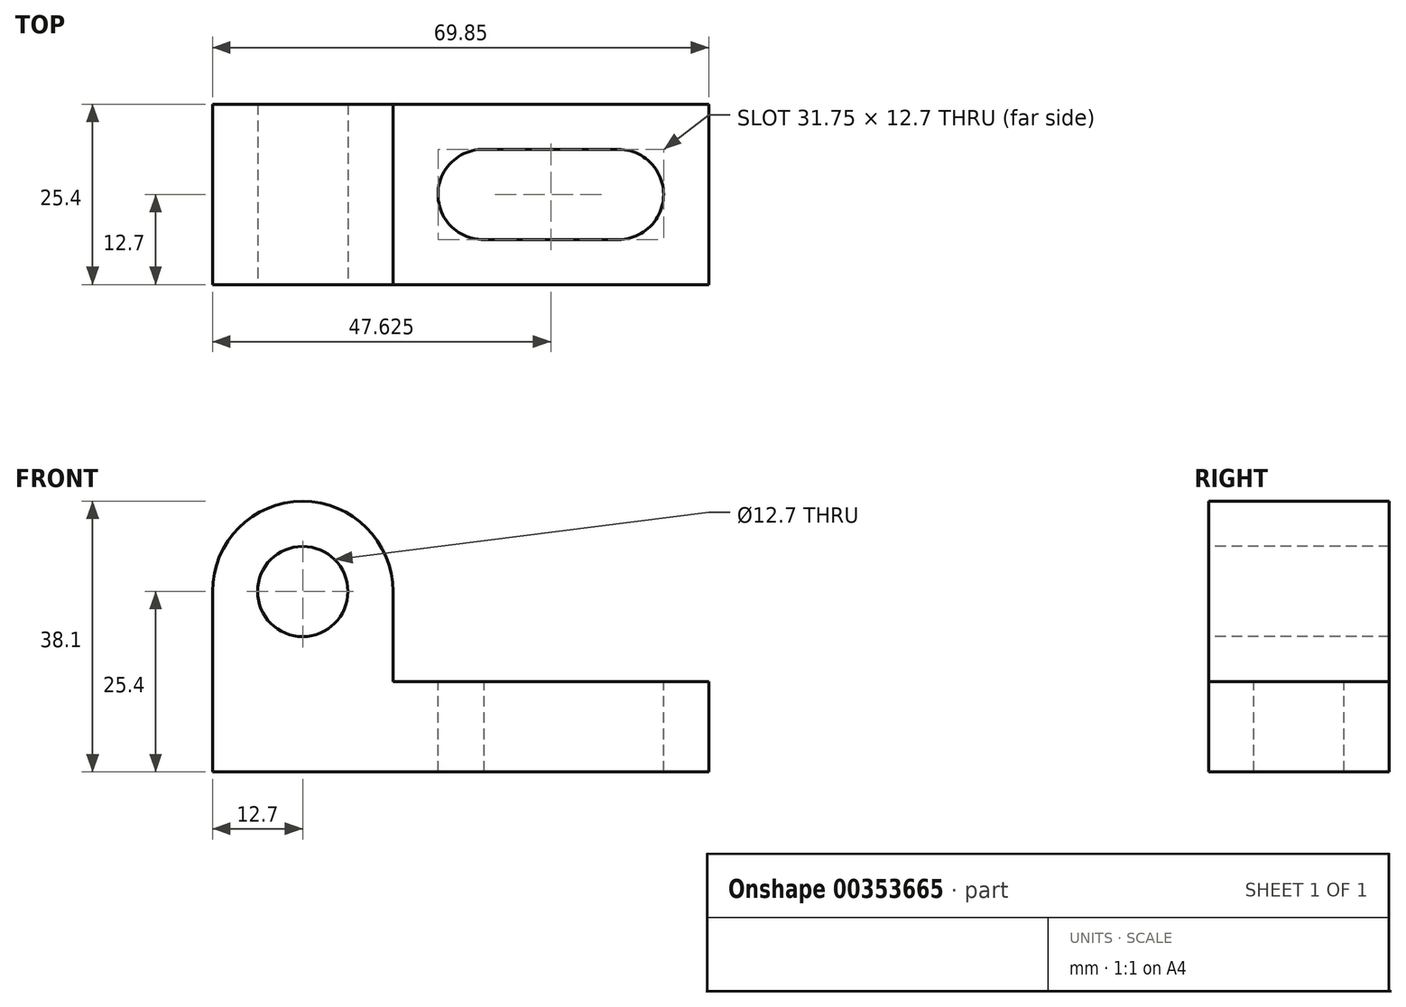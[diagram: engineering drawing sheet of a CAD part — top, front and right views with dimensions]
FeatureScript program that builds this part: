
annotation { "Feature Type Name" : "Feature", "Feature Type Description" : "" }
export const myFeature = defineFeature(function(context is Context, id is Id, definition is map)
    precondition{}
    {
        {
            var Q0;
            Q0=qCreatedBy(makeId("Front.planeOp"),FACE);
            var sketch = newSketch(context, id + "F0", { "sketchPlane" : qUnion([Q0])});
            skLineSegment(sketch, "E0", {"start": v(0, 38.1) * mm, "end": v(0, 0) * mm});
            skLineSegment(sketch, "E1", {"start": v(0, 0) * mm, "end": v(69.85, 0) * mm});
            skLineSegment(sketch, "E2", {"start": v(69.85, 0) * mm, "end": v(69.85, 12.7) * mm});
            skLineSegment(sketch, "E3", {"start": v(69.85, 12.7) * mm, "end": v(25.4, 12.7) * mm});
            skLineSegment(sketch, "E4", {"start": v(25.4, 12.7) * mm, "end": v(25.4, 38.1) * mm});
            skLineSegment(sketch, "E5", {"start": v(25.4, 38.1) * mm, "end": v(0, 38.1) * mm});
            skSolve(sketch);
        }
        {
            var Q0;
            Q0=makeQuery(id+"F0.imprint","IMPRINT",FACE,{"disambiguationData":[TD([[makeQuery(id+"F0.imprint","IMPRINT",EDGE,{"derivedFrom":sQuery(id+"F0.wireOp",EDGE,"E0")}),1.0]])]});
            extrude(context, id + "F1", {"entities" : qUnion([Q0]), "depth" : 25.4 * mm});
        }
        {
            var Q0;
            Q0=makeQuery(id+"F1.opExtrude","CAP_FACE",FACE,{"disambiguationData":[OSD([sQuery(id+"F0.wireOp",EDGE,"E0"),sQuery(id+"F0.wireOp",EDGE,"E1"),sQuery(id+"F0.wireOp",EDGE,"E2"),sQuery(id+"F0.wireOp",EDGE,"E3"),sQuery(id+"F0.wireOp",EDGE,"E4"),sQuery(id+"F0.wireOp",EDGE,"E5")])],"isStart":false});
            var sketch = newSketch(context, id + "F2", { "sketchPlane" : qUnion([Q0])});
            skCircle(sketch, "E6", {"center": v(12.7, 25.4) * mm, "radius": 6.35 * mm});
            skArc(sketch, "E7", {"start": v(25.4, 25.4) * mm, "mid": v(12.7, 38.1) * mm, "end": v(0, 25.4) * mm});
            skSolve(sketch);
        }
        {
            var Q0;
            Q0 = qSketchRegion(id + "F2", true);
            extrude(context, id + "F3", {"entities" : qUnion([Q0]), "operationType" : NewBodyOperationType.REMOVE, "oppositeDirection" : true, "depth" : 25.4 * mm});
        }
        {
            var Q0;
            {var subQ0=sQuery(id+"F2.wireOp",EDGE,"E7");var subQ1=makeQuery(id+"F1.opExtrude","CAP_EDGE",EDGE,{"disambiguationData":[OSD([sQuery(id+"F0.wireOp",EDGE,"E0")])],"isStart":false});var subQ2=makeQuery(id+"F2.imprint","INTERSECT",VERTEX,{"derivedFrom":[subQ1,subQ0]});Q0=makeQuery(id+"F2.imprint","IMPRINT",FACE,{"disambiguationData":[TD([[makeQuery(id+"F2.imprint","IMPRINT",EDGE,{"disambiguationData":[TD([[subQ2,1.0]])],"derivedFrom":subQ0}),-1.0]])]});}
            var Q1;
            {var subQ0=sQuery(id+"F2.wireOp",EDGE,"E7");var subQ1=makeQuery(id+"F1.opExtrude","CAP_EDGE",EDGE,{"disambiguationData":[OSD([sQuery(id+"F0.wireOp",EDGE,"E4")])],"isStart":false});var subQ2=makeQuery(id+"F2.imprint","INTERSECT",VERTEX,{"derivedFrom":[subQ1,subQ0]});Q1=makeQuery(id+"F2.imprint","IMPRINT",FACE,{"disambiguationData":[TD([[makeQuery(id+"F2.imprint","IMPRINT",EDGE,{"disambiguationData":[TD([[subQ2,-1.0]])],"derivedFrom":subQ0}),-1.0]])]});}
            extrude(context, id + "F4", {"entities" : qUnion([Q0, Q1]), "operationType" : NewBodyOperationType.REMOVE, "oppositeDirection" : true, "depth" : 25.4 * mm});
        }
        {
            var Q0;
            Q0=makeQuery(id+"F1.opExtrude","SWEPT_FACE",FACE,{"disambiguationData":[OSD([sQuery(id+"F0.wireOp",EDGE,"E3")])]});
            var sketch = newSketch(context, id + "F5", { "sketchPlane" : qUnion([Q0])});
            skSolve(sketch);
        }
        {
            var Q0;
            {var subQ0=sQuery(id+"F0.wireOp",EDGE,"E3");Q0=makeQuery(id+"F5.imprint","IMPRINT",FACE,{"disambiguationData":[TD([[makeQuery(id+"F5.imprint","IMPRINT",EDGE,{"derivedFrom":makeQuery(id+"F1.opExtrude","CAP_EDGE",EDGE,{"disambiguationData":[OSD([subQ0])],"isStart":true})}),1.0]])]});}
            var sketch = newSketch(context, id + "F6", { "sketchPlane" : qUnion([Q0])});
            skCircle(sketch, "E8", {"center": v(38.1, -12.7) * mm, "radius": 6.35 * mm});
            skCircle(sketch, "E9", {"center": v(57.15, -12.7) * mm, "radius": 6.35 * mm});
            skLineSegment(sketch, "E10", {"start": v(38.25, -6.35) * mm, "end": v(57.15, -6.35) * mm});
            skLineSegment(sketch, "E11", {"start": v(37.94, -19.05) * mm, "end": v(57.15, -19.05) * mm});
            skSolve(sketch);
        }
        {
            var Q0;
            Q0 = qSketchRegion(id + "F6", true);
            extrude(context, id + "F7", {"entities" : qUnion([Q0]), "operationType" : NewBodyOperationType.REMOVE, "oppositeDirection" : true, "depth" : 12.7 * mm});
        }
    });
